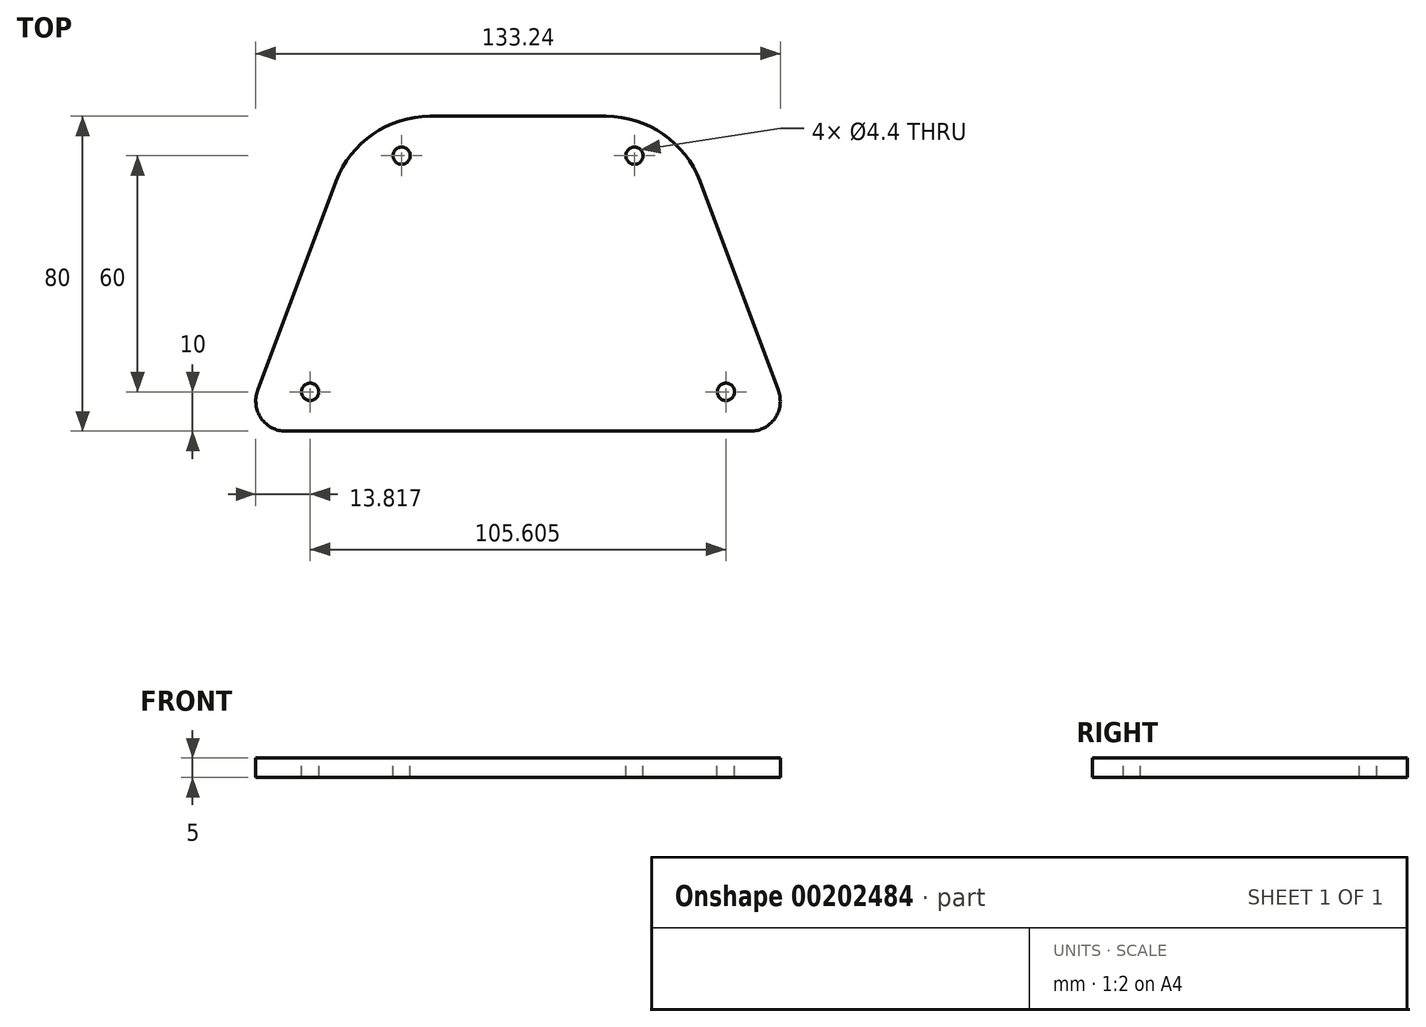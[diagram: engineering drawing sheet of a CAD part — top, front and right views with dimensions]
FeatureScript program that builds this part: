
annotation { "Feature Type Name" : "Feature", "Feature Type Description" : "" }
export const myFeature = defineFeature(function(context is Context, id is Id, definition is map)
    precondition{}
    {
        {
            var Q0;
            Q0=qCreatedBy(makeId("Top.planeOp"),FACE);
            var sketch = newSketch(context, id + "F0", { "sketchPlane" : qUnion([Q0])});
            skLineSegment(sketch, "E0", {"start": v(-70, 0) * mm, "end": v(-40, 80) * mm});
            skLineSegment(sketch, "E1", {"start": v(-40, 80) * mm, "end": v(40, 80) * mm});
            skLineSegment(sketch, "E2", {"start": v(40, 80) * mm, "end": v(70, 0) * mm});
            skLineSegment(sketch, "E3", {"start": v(70, 0) * mm, "end": v(-70, 0) * mm});
            skLineSegment(sketch, "E4", {"start": v(0, 80) * mm, "end": v(0, 0) * mm, "construction": true});
            skSolve(sketch);
        }
        {
            var Q0;
            Q0 = qSketchRegion(id + "F0", true);
            extrude(context, id + "F1", {"entities" : qUnion([Q0]), "depth" : 5 * mm});
        }
        {
            var Q0;
            Q0=makeQuery(id+"F1.opExtrude","SWEPT_EDGE",EDGE,{"disambiguationData":[OSD([sQuery(id+"F0.wireOp",EDGE,"E0"),sQuery(id+"F0.wireOp",EDGE,"E1")])]});
            var Q1;
            Q1=makeQuery(id+"F1.opExtrude","SWEPT_EDGE",EDGE,{"disambiguationData":[OSD([sQuery(id+"F0.wireOp",EDGE,"E1"),sQuery(id+"F0.wireOp",EDGE,"E2")])]});
            fillet(context, id + "F2", {"entities" : qUnion([Q0, Q1]), "radius" : 25.4 * mm, "tangentPropagation" : true, "allowEdgeOverflow" : false});
        }
        {
            var Q0;
            Q0=makeQuery(id+"F1.opExtrude","SWEPT_EDGE",EDGE,{"disambiguationData":[OSD([sQuery(id+"F0.wireOp",EDGE,"E0"),sQuery(id+"F0.wireOp",EDGE,"E3")])]});
            var Q1;
            Q1=makeQuery(id+"F1.opExtrude","SWEPT_EDGE",EDGE,{"disambiguationData":[OSD([sQuery(id+"F0.wireOp",EDGE,"E2"),sQuery(id+"F0.wireOp",EDGE,"E3")])]});
            fillet(context, id + "F3", {"entities" : qUnion([Q0, Q1]), "radius" : 7.62 * mm, "tangentPropagation" : true, "allowEdgeOverflow" : false});
        }
        {
            var Q0;
            Q0=makeQuery(id+"F1.opExtrude","CAP_FACE",FACE,{"disambiguationData":[OSD([sQuery(id+"F0.wireOp",EDGE,"E0"),sQuery(id+"F0.wireOp",EDGE,"E1"),sQuery(id+"F0.wireOp",EDGE,"E2"),sQuery(id+"F0.wireOp",EDGE,"E3")])],"isStart":false});
            var sketch = newSketch(context, id + "F4", { "sketchPlane" : qUnion([Q0])});
            skLineSegment(sketch, "E5", {"start": v(-29.58, 70) * mm, "end": v(29.58, 70) * mm, "construction": true});
            skPoint(sketch, "E6", {"position": v(0, 70) * mm});
            skLineSegment(sketch, "E7", {"start": v(-52.8, 10) * mm, "end": v(52.8, 10) * mm, "construction": true});
            skPoint(sketch, "E8", {"position": v(0, 10) * mm});
            skPoint(sketch, "E9", {"position": v(-52.8, 10) * mm});
            skPoint(sketch, "E10", {"position": v(-29.58, 70) * mm});
            skPoint(sketch, "E11", {"position": v(29.58, 70) * mm});
            skPoint(sketch, "E12", {"position": v(52.8, 10) * mm});
            skSolve(sketch);
        }
        {
            var Q0;
            Q0=sQuery(id+"F4.wireOp",VERTEX,"E10");
            var Q1;
            Q1=sQuery(id+"F4.wireOp",VERTEX,"E11");
            var Q2;
            Q2=sQuery(id+"F4.wireOp",VERTEX,"E12");
            var Q3;
            Q3=sQuery(id+"F4.wireOp",VERTEX,"E9");
            var Q4;
            Q4=makeQuery(id+"F1.opExtrude","SWEPT_BODY",BODY,{"disambiguationData":[OSD([sQuery(id+"F0.wireOp",EDGE,"E0"),sQuery(id+"F0.wireOp",EDGE,"E1"),sQuery(id+"F0.wireOp",EDGE,"E2"),sQuery(id+"F0.wireOp",EDGE,"E3")])]});
            hole(context, id + "F5", {"style" : HoleStyle.SIMPLE, "endStyle" : HoleEndStyle.THROUGH, "standardTappedOrClearance" : lookupTablePath({ "standard" : "ISO", "fit" : "Normal", "size" : "M4", "type" : "Clearance" }), "standardBlindInLast" : lookupTablePath({ "fit" : "Standard", "standard" : "ISO", "size" : "M4", "type" : "Clearance" }), "holeDiameter" : 4.4 * mm, "locations" : qUnion([Q0, Q1, Q2, Q3]), "scope" : qUnion([Q4]), "isTappedThrough" : true});
        }
    });
